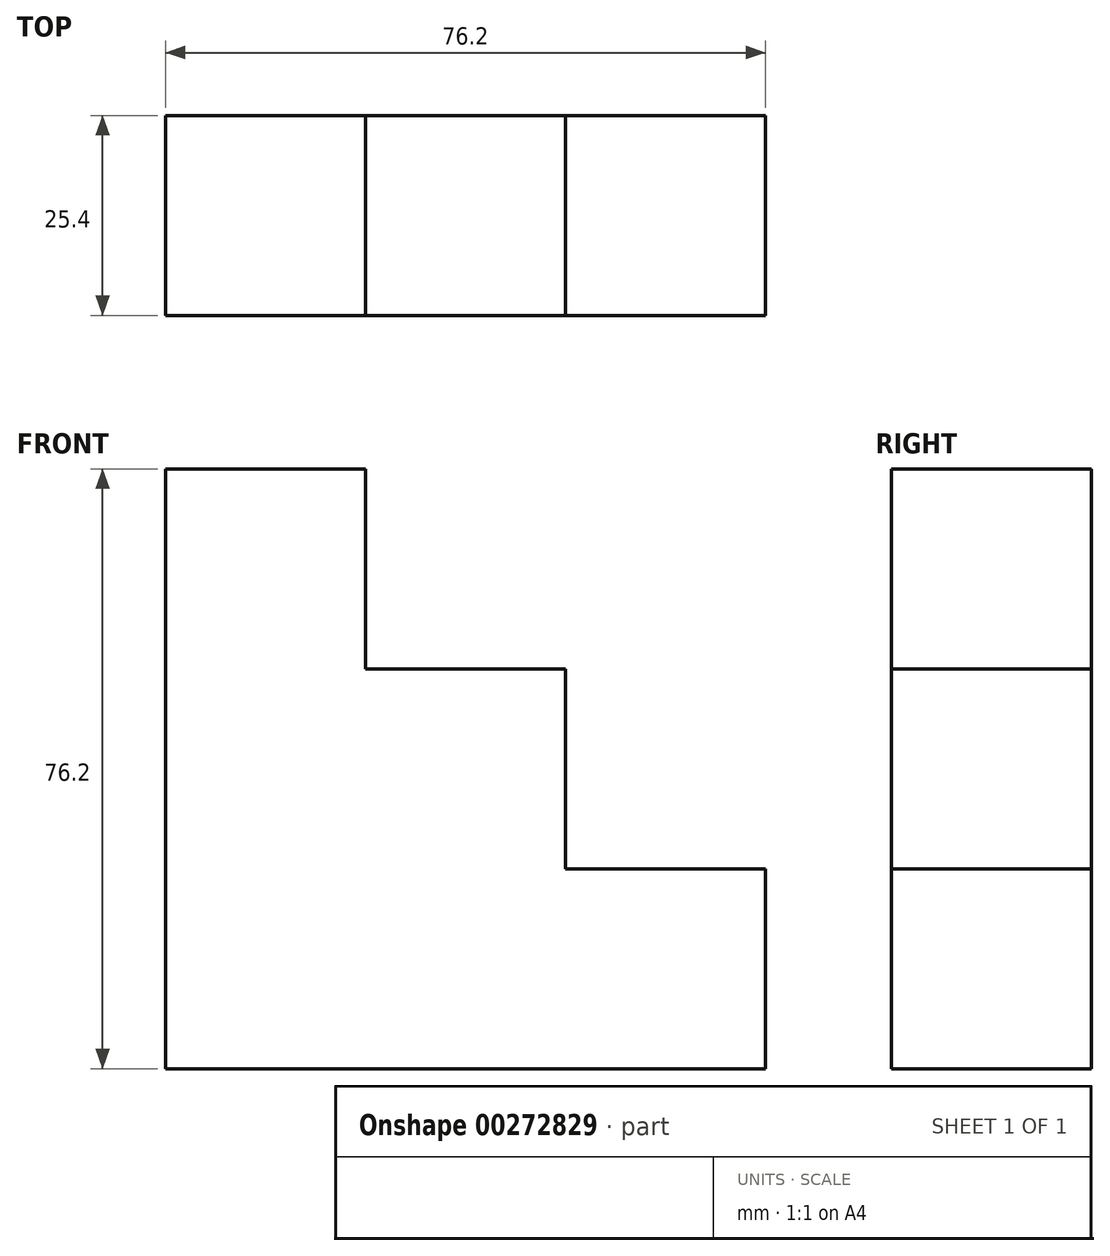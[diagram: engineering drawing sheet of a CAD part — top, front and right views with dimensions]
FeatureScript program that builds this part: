
annotation { "Feature Type Name" : "Feature", "Feature Type Description" : "" }
export const myFeature = defineFeature(function(context is Context, id is Id, definition is map)
    precondition{}
    {
        {
            var Q0;
            Q0=qCreatedBy(makeId("Front.planeOp"),FACE);
            var sketch = newSketch(context, id + "F0", { "sketchPlane" : qUnion([Q0])});
            skLineSegment(sketch, "E0", {"start": v(0, 0) * mm, "end": v(-76.2, 0) * mm});
            skLineSegment(sketch, "E1", {"start": v(-76.2, 0) * mm, "end": v(-76.2, 76.2) * mm});
            skLineSegment(sketch, "E2", {"start": v(-76.2, 76.2) * mm, "end": v(-50.8, 76.2) * mm});
            skLineSegment(sketch, "E3", {"start": v(-50.8, 76.2) * mm, "end": v(-50.8, 50.8) * mm});
            skLineSegment(sketch, "E4", {"start": v(-50.8, 50.8) * mm, "end": v(-25.4, 50.8) * mm});
            skLineSegment(sketch, "E5", {"start": v(-25.4, 50.8) * mm, "end": v(-25.4, 25.4) * mm});
            skLineSegment(sketch, "E6", {"start": v(-25.4, 25.4) * mm, "end": v(0, 25.4) * mm});
            skLineSegment(sketch, "E7", {"start": v(0, 25.4) * mm, "end": v(0, 0) * mm});
            skSolve(sketch);
        }
        {
            var Q0;
            Q0=makeQuery(id+"F0.imprint","IMPRINT",FACE,{"disambiguationData":[TD([[makeQuery(id+"F0.imprint","IMPRINT",EDGE,{"derivedFrom":sQuery(id+"F0.wireOp",EDGE,"E0")}),-1.0]])]});
            extrude(context, id + "F1", {"entities" : qUnion([Q0]), "depth" : 25.4 * mm});
        }
    });
